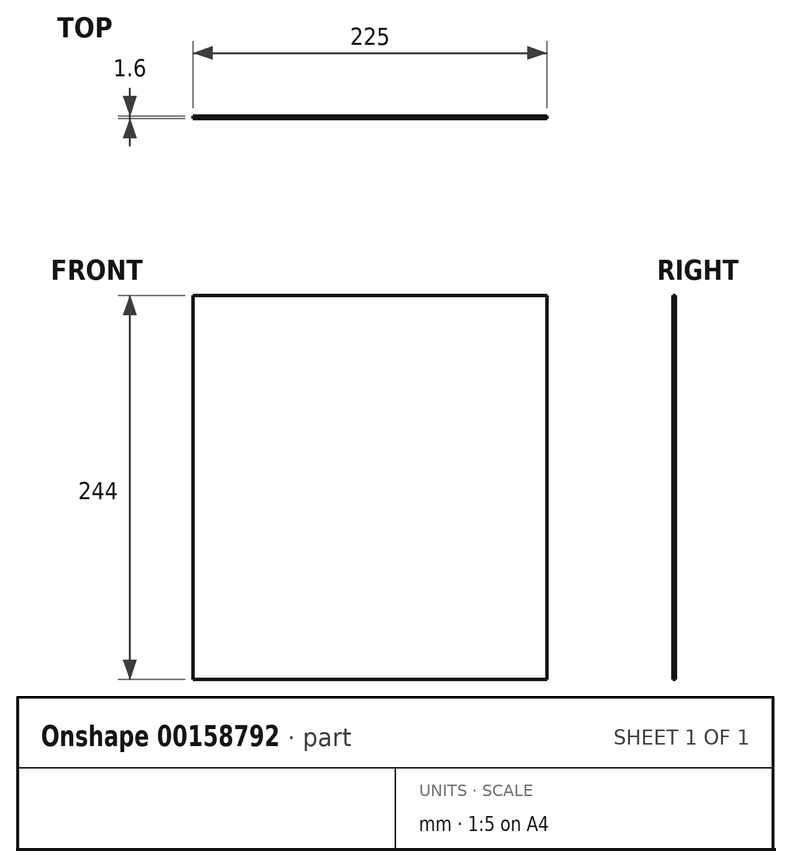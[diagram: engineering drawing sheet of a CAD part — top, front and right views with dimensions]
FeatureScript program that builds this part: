
annotation { "Feature Type Name" : "Feature", "Feature Type Description" : "" }
export const myFeature = defineFeature(function(context is Context, id is Id, definition is map)
    precondition{}
    {
        {
            var Q0;
            Q0=qCreatedBy(makeId("Front.planeOp"),FACE);
            var sketch = newSketch(context, id + "F0", { "sketchPlane" : qUnion([Q0])});
            skLineSegment(sketch, "E0.bottom", {"start": v(112.5, 122) * mm, "end": v(-112.5, 122) * mm});
            skLineSegment(sketch, "E0.top", {"start": v(112.5, -122) * mm, "end": v(-112.5, -122) * mm});
            skLineSegment(sketch, "E0.left", {"start": v(112.5, 122) * mm, "end": v(112.5, -122) * mm});
            skLineSegment(sketch, "E0.right", {"start": v(-112.5, 122) * mm, "end": v(-112.5, -122) * mm});
            skPoint(sketch, "E0.middle", {"position": v(0, 0) * mm});
            skSolve(sketch);
        }
        {
            var Q0;
            Q0 = qSketchRegion(id + "F0", true);
            extrude(context, id + "F1", {"entities" : qUnion([Q0]), "depth" : 1.6 * mm});
        }
    });
